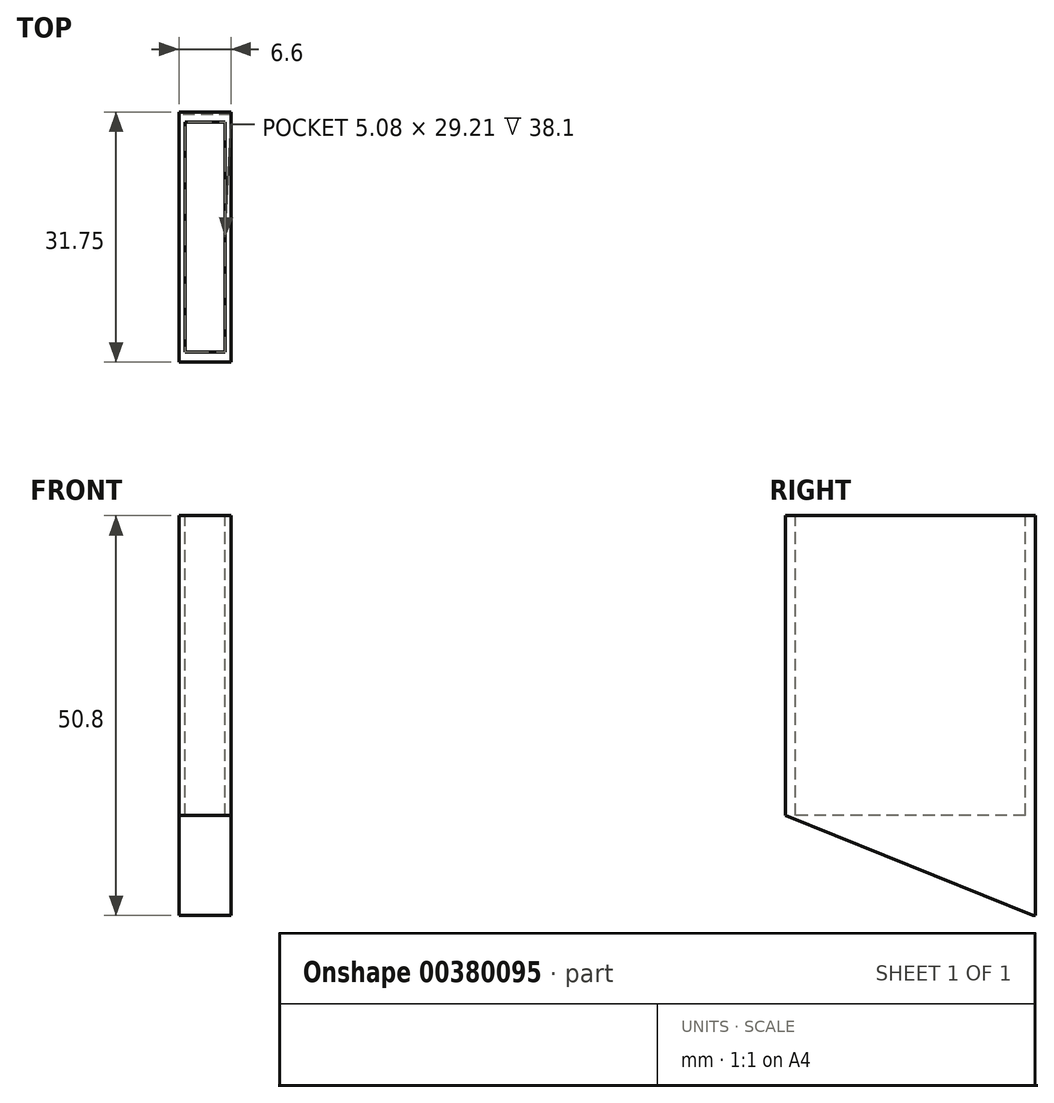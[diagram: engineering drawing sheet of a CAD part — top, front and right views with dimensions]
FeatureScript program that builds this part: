
annotation { "Feature Type Name" : "Feature", "Feature Type Description" : "" }
export const myFeature = defineFeature(function(context is Context, id is Id, definition is map)
    precondition{}
    {
        {
            var Q0;
            Q0=qCreatedBy(makeId("Right.planeOp"),FACE);
            var sketch = newSketch(context, id + "F0", { "sketchPlane" : qUnion([Q0])});
            skLineSegment(sketch, "E0", {"start": v(0, 21.9) * mm, "end": v(-31.75, 21.9) * mm});
            skLineSegment(sketch, "E1", {"start": v(0, 21.9) * mm, "end": v(0, -28.9) * mm});
            skLineSegment(sketch, "E2", {"start": v(-31.75, 21.9) * mm, "end": v(-31.75, -28.9) * mm});
            skLineSegment(sketch, "E3", {"start": v(-31.75, -28.9) * mm, "end": v(0, -28.9) * mm});
            skSolve(sketch);
        }
        {
            var Q0;
            Q0 = qSketchRegion(id + "F0", true);
            extrude(context, id + "F1", {"entities" : qUnion([Q0]), "depth" : 6.6 * mm});
        }
        {
            var Q0;
            Q0=makeQuery(id+"F1.opExtrude","SWEPT_EDGE",EDGE,{"disambiguationData":[OSD([sQuery(id+"F0.wireOp",EDGE,"E2"),sQuery(id+"F0.wireOp",EDGE,"E3")])]});
            chamfer(context, id + "F2", {"entities" : qUnion([Q0]), "chamferType" : ChamferType.OFFSET_ANGLE, "width" : 12.7 * mm, "oppositeDirection" : true, "angle" : 68 * degree, "tangentPropagation" : true});
        }
        {
            var Q0;
            Q0=makeQuery(id+"F1.opExtrude","SWEPT_FACE",FACE,{"disambiguationData":[OSD([sQuery(id+"F0.wireOp",EDGE,"E0")])]});
            var sketch = newSketch(context, id + "F3", { "sketchPlane" : qUnion([Q0])});
            skLineSegment(sketch, "E4", {"start": v(3.3, 0) * mm, "end": v(3.3, -1.27) * mm});
            skLineSegment(sketch, "E5", {"start": v(3.3, -31.75) * mm, "end": v(3.3, -30.48) * mm});
            skLineSegment(sketch, "E6", {"start": v(3.3, -30.48) * mm, "end": v(5.84, -30.48) * mm});
            skLineSegment(sketch, "E7", {"start": v(3.3, -30.48) * mm, "end": v(0.76, -30.48) * mm});
            skLineSegment(sketch, "E8", {"start": v(3.3, -1.27) * mm, "end": v(5.84, -1.27) * mm});
            skLineSegment(sketch, "E9", {"start": v(3.3, -1.27) * mm, "end": v(0.76, -1.27) * mm});
            skLineSegment(sketch, "E10", {"start": v(0.76, -30.48) * mm, "end": v(0.76, -1.27) * mm});
            skLineSegment(sketch, "E11", {"start": v(5.84, -1.27) * mm, "end": v(5.84, -30.48) * mm});
            skSolve(sketch);
        }
        {
            var Q0;
            Q0 = qSketchRegion(id + "F3", true);
            extrude(context, id + "F4", {"entities" : qUnion([Q0]), "operationType" : NewBodyOperationType.REMOVE, "oppositeDirection" : true, "depth" : 38.1 * mm});
        }
    });
